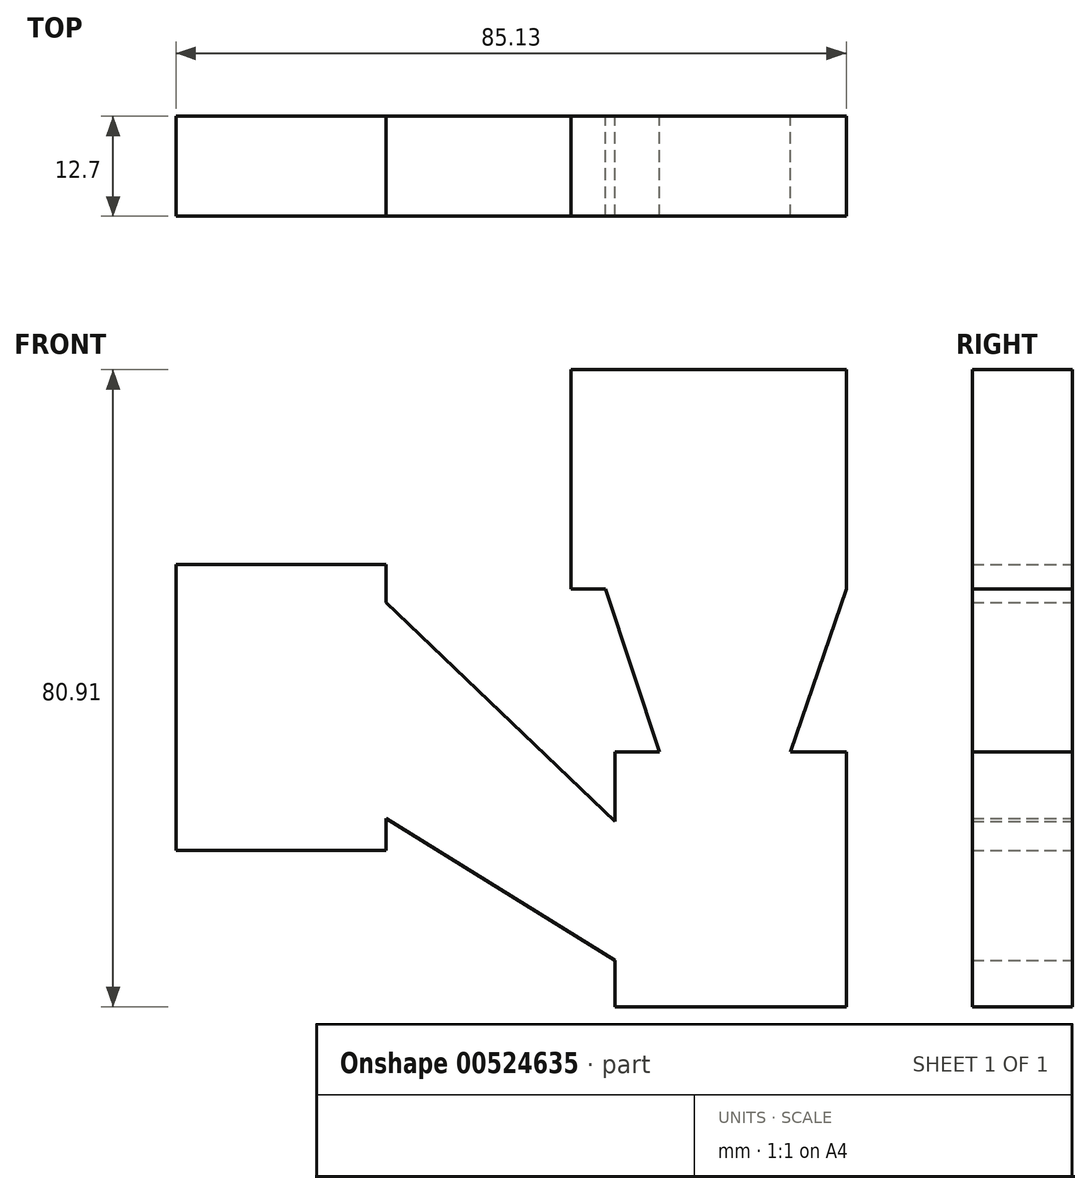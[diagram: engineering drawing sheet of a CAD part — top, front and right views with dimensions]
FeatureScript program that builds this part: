
annotation { "Feature Type Name" : "Feature", "Feature Type Description" : "" }
export const myFeature = defineFeature(function(context is Context, id is Id, definition is map)
    precondition{}
    {
        {
            var Q0;
            Q0=qCreatedBy(makeId("Front.planeOp"),FACE);
            var sketch = newSketch(context, id + "F0", { "sketchPlane" : qUnion([Q0])});
            skLineSegment(sketch, "E0.bottom", {"start": v(-129.29, 63.96) * mm, "end": v(-102.62, 63.96) * mm});
            skLineSegment(sketch, "E0.top", {"start": v(-129.29, 27.62) * mm, "end": v(-102.62, 27.62) * mm});
            skLineSegment(sketch, "E0.left", {"start": v(-129.29, 63.96) * mm, "end": v(-129.29, 27.62) * mm});
            skLineSegment(sketch, "E0.right", {"start": v(-102.62, 63.96) * mm, "end": v(-102.62, 27.62) * mm});
            skLineSegment(sketch, "E1.bottom", {"start": v(-73.51, 40.18) * mm, "end": v(-44.16, 40.18) * mm});
            skLineSegment(sketch, "E1.top", {"start": v(-73.51, 7.8) * mm, "end": v(-44.16, 7.8) * mm});
            skLineSegment(sketch, "E1.left", {"start": v(-73.51, 40.18) * mm, "end": v(-73.51, 7.8) * mm});
            skLineSegment(sketch, "E1.right", {"start": v(-44.16, 40.18) * mm, "end": v(-44.16, 7.8) * mm});
            skLineSegment(sketch, "E2", {"start": v(-73.51, 31.3) * mm, "end": v(-102.62, 59.18) * mm});
            skLineSegment(sketch, "E3", {"start": v(-73.51, 13.7) * mm, "end": v(-102.62, 31.7) * mm});
            skLineSegment(sketch, "E4.bottom", {"start": v(-44.16, 60.89) * mm, "end": v(-79.14, 60.89) * mm});
            skLineSegment(sketch, "E4.top", {"start": v(-44.16, 88.7) * mm, "end": v(-79.14, 88.7) * mm});
            skLineSegment(sketch, "E4.left", {"start": v(-44.16, 60.89) * mm, "end": v(-44.16, 88.7) * mm});
            skLineSegment(sketch, "E4.right", {"start": v(-79.14, 60.89) * mm, "end": v(-79.14, 88.7) * mm});
            skLineSegment(sketch, "E5", {"start": v(-67.89, 40.18) * mm, "end": v(-74.74, 60.89) * mm});
            skLineSegment(sketch, "E6", {"start": v(-51.25, 40.18) * mm, "end": v(-44.16, 60.89) * mm});
            skSolve(sketch);
        }
        {
            var Q0;
            Q0=makeQuery(id+"F0.imprint","IMPRINT",FACE,{"disambiguationData":[TD([[makeQuery(id+"F0.imprint","IMPRINT",EDGE,{"derivedFrom":sQuery(id+"F0.wireOp",EDGE,"E4.top")}),1.0]])]});
            var Q1;
            {var subQ1=sQuery(id+"F0.wireOp",EDGE,"E0.bottom");Q1=makeQuery(id+"F0.imprint","IMPRINT",FACE,{"disambiguationData":[TD([[makeQuery(id+"F0.imprint","IMPRINT",EDGE,{"derivedFrom":subQ1}),-1.0]])]});}
            var Q2;
            {var subQ0=sQuery(id+"F0.wireOp",EDGE,"E1.top");Q2=makeQuery(id+"F0.imprint","IMPRINT",FACE,{"disambiguationData":[TD([[makeQuery(id+"F0.imprint","IMPRINT",EDGE,{"derivedFrom":subQ0}),1.0]])]});}
            var Q3;
            {var subQ0=sQuery(id+"F0.wireOp",EDGE,"E2");Q3=makeQuery(id+"F0.imprint","IMPRINT",FACE,{"disambiguationData":[TD([[makeQuery(id+"F0.imprint","IMPRINT",EDGE,{"derivedFrom":subQ0}),1.0]])]});}
            var Q4;
            {var subQ0=sQuery(id+"F0.wireOp",EDGE,"E5");Q4=makeQuery(id+"F0.imprint","IMPRINT",FACE,{"disambiguationData":[TD([[makeQuery(id+"F0.imprint","IMPRINT",EDGE,{"derivedFrom":subQ0}),-1.0]])]});}
            extrude(context, id + "F1", {"entities" : qUnion([Q0, Q1, Q2, Q3, Q4]), "depth" : 12.7 * mm, "offsetDistance" : 25.4 * mm});
        }
    });
